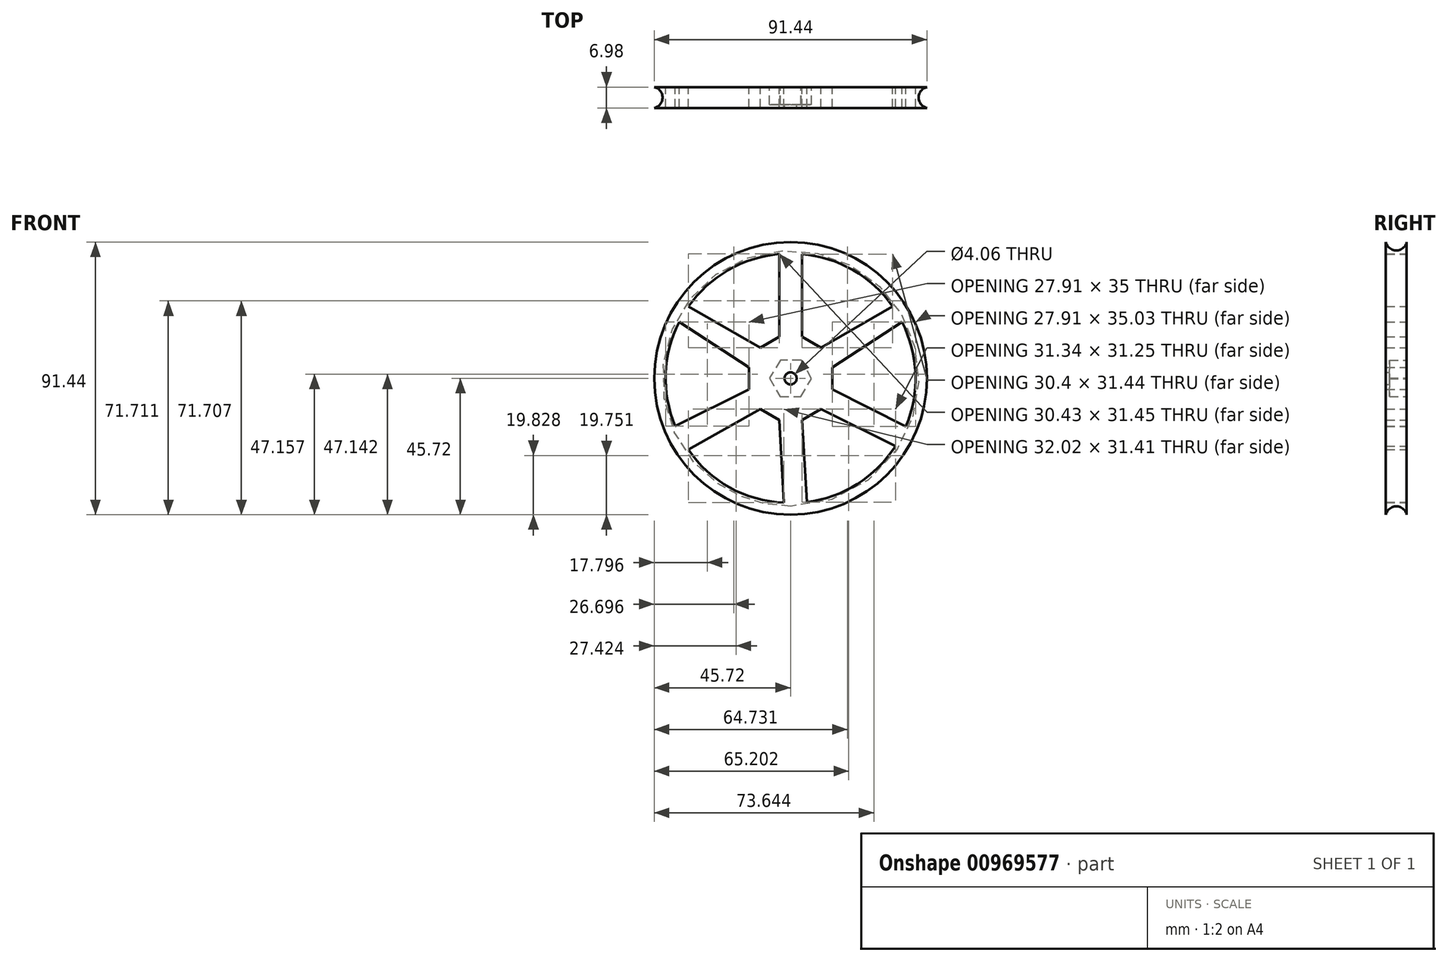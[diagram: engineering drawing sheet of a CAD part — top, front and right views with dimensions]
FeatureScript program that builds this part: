
annotation { "Feature Type Name" : "Feature", "Feature Type Description" : "" }
export const myFeature = defineFeature(function(context is Context, id is Id, definition is map)
    precondition{}
    {
        {
            var Q0;
            Q0=qCreatedBy(makeId("Top.planeOp"),FACE);
            var sketch = newSketch(context, id + "F0", { "sketchPlane" : qUnion([Q0])});
            skLineSegment(sketch, "E0", {"start": v(0, -13.42) * mm, "end": v(0, -13.23) * mm});
            skLineSegment(sketch, "E1", {"start": v(0, -13.42) * mm, "end": v(45.72, -13.42) * mm});
            skLineSegment(sketch, "E2", {"start": v(0, -3.9) * mm, "end": v(45.74, -3.9) * mm});
            skLineSegment(sketch, "E3", {"start": v(0, -13.23) * mm, "end": v(0, -3.9) * mm});
            skLineSegment(sketch, "E4", {"start": v(0, -5.17) * mm, "end": v(45.72, -5.17) * mm});
            skLineSegment(sketch, "E5", {"start": v(45.72, -12.15) * mm, "end": v(0, -12.15) * mm});
            skArc(sketch, "E6", {"start": v(45.72, -5.17) * mm, "mid": v(42.91, -8.66) * mm, "end": v(45.72, -12.15) * mm});
            skSolve(sketch);
        }
        {
            var Q0;
            {var subQ4=sQuery(id+"F0.wireOp",EDGE,"E0");Q0=makeQuery(id+"F0.imprint","IMPRINT",FACE,{"disambiguationData":[TD([[makeQuery(id+"F0.imprint","IMPRINT",EDGE,{"derivedFrom":subQ4}),-1.0]])]});}
            var Q1;
            {var subQ5=sQuery(id+"F0.wireOp",EDGE,"E4");Q1=makeQuery(id+"F0.imprint","IMPRINT",FACE,{"disambiguationData":[TD([[makeQuery(id+"F0.imprint","IMPRINT",EDGE,{"derivedFrom":subQ5}),1.0]])]});}
            var Q2;
            {var subQ0=sQuery(id+"F0.wireOp",EDGE,"E4");Q2=makeQuery(id+"F0.imprint","IMPRINT",FACE,{"disambiguationData":[TD([[makeQuery(id+"F0.imprint","IMPRINT",EDGE,{"derivedFrom":subQ0}),-1.0]])]});}
            var Q3;
            Q3=sQuery(id+"F0.wireOp",EDGE,"E3");
            revolve(context, id + "F1", {"surfaceOperationType" : NewSurfaceOperationType.NEW, "entities" : qUnion([Q0, Q1, Q2]), "axis" : qUnion([Q3]), "revolveType" : RevolveType.FULL});
        }
        {
            var Q0;
            Q0=qCreatedBy(makeId("Front.planeOp"),FACE);
            var sketch = newSketch(context, id + "F2", { "sketchPlane" : qUnion([Q0])});
            skCircle(sketch, "E7", {"center": v(0, 0) * mm, "radius": 44.45 * mm});
            skCircle(sketch, "E8.cCircle", {"center": v(0, 0) * mm, "radius": 13.97 * mm, "construction": true});
            skLineSegment(sketch, "E8.0", {"start": v(-13.97, -8.07) * mm, "end": v(-13.97, 8.07) * mm});
            skLineSegment(sketch, "E8.1", {"start": v(-13.97, 8.07) * mm, "end": v(0, 16.13) * mm});
            skLineSegment(sketch, "E8.2", {"start": v(0, 16.13) * mm, "end": v(13.97, 8.07) * mm});
            skLineSegment(sketch, "E8.3", {"start": v(13.97, 8.07) * mm, "end": v(13.97, -8.07) * mm});
            skLineSegment(sketch, "E8.4", {"start": v(13.97, -8.07) * mm, "end": v(0, -16.13) * mm});
            skLineSegment(sketch, "E8.5", {"start": v(0, -16.13) * mm, "end": v(-13.97, -8.07) * mm});
            skLineSegment(sketch, "E9", {"start": v(-10.16, -10.27) * mm, "end": v(-34.3, -23.84) * mm});
            skLineSegment(sketch, "E10", {"start": v(-38.69, -16.06) * mm, "end": v(-13.97, -3.67) * mm});
            skLineSegment(sketch, "E11", {"start": v(-3.81, -13.93) * mm, "end": v(-2.29, -41.67) * mm});
            skLineSegment(sketch, "E12", {"start": v(3.81, -13.93) * mm, "end": v(5.44, -41.52) * mm});
            skLineSegment(sketch, "E13", {"start": v(10.16, -10.27) * mm, "end": v(35.15, -22.77) * mm});
            skLineSegment(sketch, "E14", {"start": v(13.97, -3.67) * mm, "end": v(38.68, -16.1) * mm});
            skLineSegment(sketch, "E15", {"start": v(13.97, 3.67) * mm, "end": v(37.33, 18.94) * mm});
            skLineSegment(sketch, "E16", {"start": v(10.16, 10.27) * mm, "end": v(34.21, 24.15) * mm});
            skLineSegment(sketch, "E17", {"start": v(-10.16, 10.27) * mm, "end": v(-34.24, 24.1) * mm});
            skLineSegment(sketch, "E18", {"start": v(-13.97, 3.67) * mm, "end": v(-37.34, 18.94) * mm});
            skLineSegment(sketch, "E19", {"start": v(3.81, 13.93) * mm, "end": v(3.81, 41.7) * mm});
            skLineSegment(sketch, "E20", {"start": v(-3.8, 13.93) * mm, "end": v(-3.81, 41.72) * mm});
            skArc(sketch, "E21", {"start": v(25.84, 35.93) * mm, "mid": v(22.12, 38.32) * mm, "end": v(18.2, 40.34) * mm});
            skCircle(sketch, "E22", {"center": v(0, 0) * mm, "radius": 2.03 * mm});
            skPoint(sketch, "E23.visualSharp", {"position": v(36.45, 25.44) * mm});
            skPoint(sketch, "E24.visualSharp", {"position": v(39.51, 20.36) * mm});
            skPoint(sketch, "E25.visualSharp", {"position": v(-3.81, 44.29) * mm});
            skPoint(sketch, "E26.visualSharp", {"position": v(3.81, 44.29) * mm});
            skPoint(sketch, "E27.visualSharp", {"position": v(-36.49, 25.39) * mm});
            skPoint(sketch, "E28.visualSharp", {"position": v(-39.51, 20.36) * mm});
            skPoint(sketch, "E29.visualSharp", {"position": v(-40.98, -17.21) * mm});
            skPoint(sketch, "E30.visualSharp", {"position": v(-36.64, -25.16) * mm});
            skPoint(sketch, "E31.visualSharp", {"position": v(-2.14, -44.4) * mm});
            skPoint(sketch, "E32.visualSharp", {"position": v(5.6, -44.1) * mm});
            skPoint(sketch, "E33.visualSharp", {"position": v(37.46, -23.93) * mm});
            skPoint(sketch, "E34.visualSharp", {"position": v(40.97, -17.24) * mm});
            skCircle(sketch, "E35.cCircle", {"center": v(0, 0) * mm, "radius": 6.1 * mm, "construction": true});
            skPoint(sketch, "E35.0.midPoint", {"position": v(-6.1, 0) * mm});
            skArc(sketch, "E36", {"start": v(38.68, -16.1) * mm, "mid": v(41.88, 1.57) * mm, "end": v(37.33, 18.94) * mm});
            skArc(sketch, "E37", {"start": v(34.21, 24.15) * mm, "mid": v(20.95, 36.3) * mm, "end": v(3.81, 41.7) * mm});
            skArc(sketch, "E38", {"start": v(-3.8, 41.72) * mm, "mid": v(-20.98, 36.28) * mm, "end": v(-34.24, 24.1) * mm});
            skArc(sketch, "E39", {"start": v(-37.34, 18.94) * mm, "mid": v(-41.88, 1.59) * mm, "end": v(-38.69, -16.06) * mm});
            skArc(sketch, "E40", {"start": v(-34.3, -23.84) * mm, "mid": v(-20.43, -36.6) * mm, "end": v(-2.29, -41.67) * mm});
            skArc(sketch, "E41", {"start": v(5.44, -41.52) * mm, "mid": v(22.37, -35.44) * mm, "end": v(35.15, -22.77) * mm});
            skPoint(sketch, "E42.startSnap0", {"position": v(-22.2, 17.18) * mm});
            skLineSegment(sketch, "E43", {"start": v(-28.4, -18.27) * mm, "end": v(-28.03, -18.13) * mm});
            skLineSegment(sketch, "E44", {"start": v(-30.08, -13.81) * mm, "end": v(-29.7, -13.7) * mm});
            skLineSegment(sketch, "E45", {"start": v(-33.78, -18) * mm, "end": v(-33.93, -17.63) * mm});
            skLineSegment(sketch, "E46", {"start": v(-26.41, -22.88) * mm, "end": v(-26.41, -23.36) * mm});
            skLineSegment(sketch, "E47.0", {"start": v(-3.58, -6.06) * mm, "end": v(-7.04, 0.07) * mm});
            skLineSegment(sketch, "E47.1", {"start": v(-7.04, 0.07) * mm, "end": v(-3.46, 6.13) * mm});
            skLineSegment(sketch, "E47.2", {"start": v(-3.46, 6.13) * mm, "end": v(3.58, 6.06) * mm});
            skLineSegment(sketch, "E47.3", {"start": v(3.58, 6.06) * mm, "end": v(7.04, -0.07) * mm});
            skLineSegment(sketch, "E47.4", {"start": v(7.04, -0.07) * mm, "end": v(3.46, -6.13) * mm});
            skLineSegment(sketch, "E47.5", {"start": v(3.46, -6.13) * mm, "end": v(-3.58, -6.06) * mm});
            skPoint(sketch, "E47.0.midPoint", {"position": v(-5.31, -3) * mm});
            skSolve(sketch);
        }
        {
            var Q0;
            {var subQ0=sQuery(id+"F2.wireOp",EDGE,"E14");Q0=makeQuery(id+"F2.imprint","IMPRINT",FACE,{"disambiguationData":[TD([[makeQuery(id+"F2.imprint","IMPRINT",EDGE,{"derivedFrom":subQ0}),1.0]])]});}
            var Q1;
            {var subQ0=sQuery(id+"F2.wireOp",EDGE,"E16");Q1=makeQuery(id+"F2.imprint","IMPRINT",FACE,{"disambiguationData":[TD([[makeQuery(id+"F2.imprint","IMPRINT",EDGE,{"derivedFrom":subQ0}),1.0]])]});}
            var Q2;
            {var subQ0=sQuery(id+"F2.wireOp",EDGE,"E17");Q2=makeQuery(id+"F2.imprint","IMPRINT",FACE,{"disambiguationData":[TD([[makeQuery(id+"F2.imprint","IMPRINT",EDGE,{"derivedFrom":subQ0}),-1.0]])]});}
            var Q3;
            {var subQ0=sQuery(id+"F2.wireOp",EDGE,"E10");Q3=makeQuery(id+"F2.imprint","IMPRINT",FACE,{"disambiguationData":[TD([[makeQuery(id+"F2.imprint","IMPRINT",EDGE,{"derivedFrom":subQ0}),1.0]])]});}
            var Q4;
            {var subQ0=sQuery(id+"F2.wireOp",EDGE,"E9");Q4=makeQuery(id+"F2.imprint","IMPRINT",FACE,{"disambiguationData":[TD([[makeQuery(id+"F2.imprint","IMPRINT",EDGE,{"derivedFrom":subQ0}),1.0]])]});}
            var Q5;
            {var subQ0=sQuery(id+"F2.wireOp",EDGE,"E12");Q5=makeQuery(id+"F2.imprint","IMPRINT",FACE,{"disambiguationData":[TD([[makeQuery(id+"F2.imprint","IMPRINT",EDGE,{"derivedFrom":subQ0}),1.0]])]});}
            var Q6;
            Q6=makeQuery(id+"F2.imprint","IMPRINT",FACE,{"disambiguationData":[TD([[makeQuery(id+"F2.imprint","IMPRINT",EDGE,{"derivedFrom":sQuery(id+"F2.wireOp",EDGE,"E22")}),1.0]])]});
            extrude(context, id + "F3", {"entities" : qUnion([Q0, Q1, Q2, Q3, Q4, Q5, Q6]), "operationType" : NewBodyOperationType.REMOVE, "depth" : 15.88 * mm, "offsetDistance" : 25.4 * mm});
        }
        {
            var Q0;
            Q0=makeQuery(id+"F2.imprint","IMPRINT",FACE,{"disambiguationData":[TD([[makeQuery(id+"F2.imprint","IMPRINT",EDGE,{"derivedFrom":sQuery(id+"F2.wireOp",EDGE,"E22")}),-1.0]])]});
            var Q1;
            Q1=makeQuery(id+"F2.imprint","IMPRINT",FACE,{"disambiguationData":[TD([[makeQuery(id+"F2.imprint","IMPRINT",EDGE,{"derivedFrom":sQuery(id+"F2.wireOp",EDGE,"cEWQKaYX-tMYh-FtrB-USuR-naG5t3EE6AXz")}),1.0]])]});
            var Q2;
            {var subQ0=sQuery(id+"F2.wireOp",EDGE,"qJgOAMjh-opkx-zOsv-M7fw-z26SiIDsqRWk");Q2=makeQuery(id+"F2.imprint","IMPRINT",FACE,{"disambiguationData":[TD([[makeQuery(id+"F2.imprint","IMPRINT",EDGE,{"derivedFrom":subQ0}),-1.0]])]});}
            var Q3;
            {var subQ0=sQuery(id+"F2.wireOp",EDGE,"E43");Q3=makeQuery(id+"F2.imprint","IMPRINT",FACE,{"disambiguationData":[TD([[makeQuery(id+"F2.imprint","IMPRINT",EDGE,{"derivedFrom":subQ0}),1.0]])]});}
            extrude(context, id + "F4", {"entities" : qUnion([Q0, Q1, Q2, Q3]), "operationType" : NewBodyOperationType.REMOVE, "depth" : 11 * mm, "offsetDistance" : 25.4 * mm});
        }
    });
